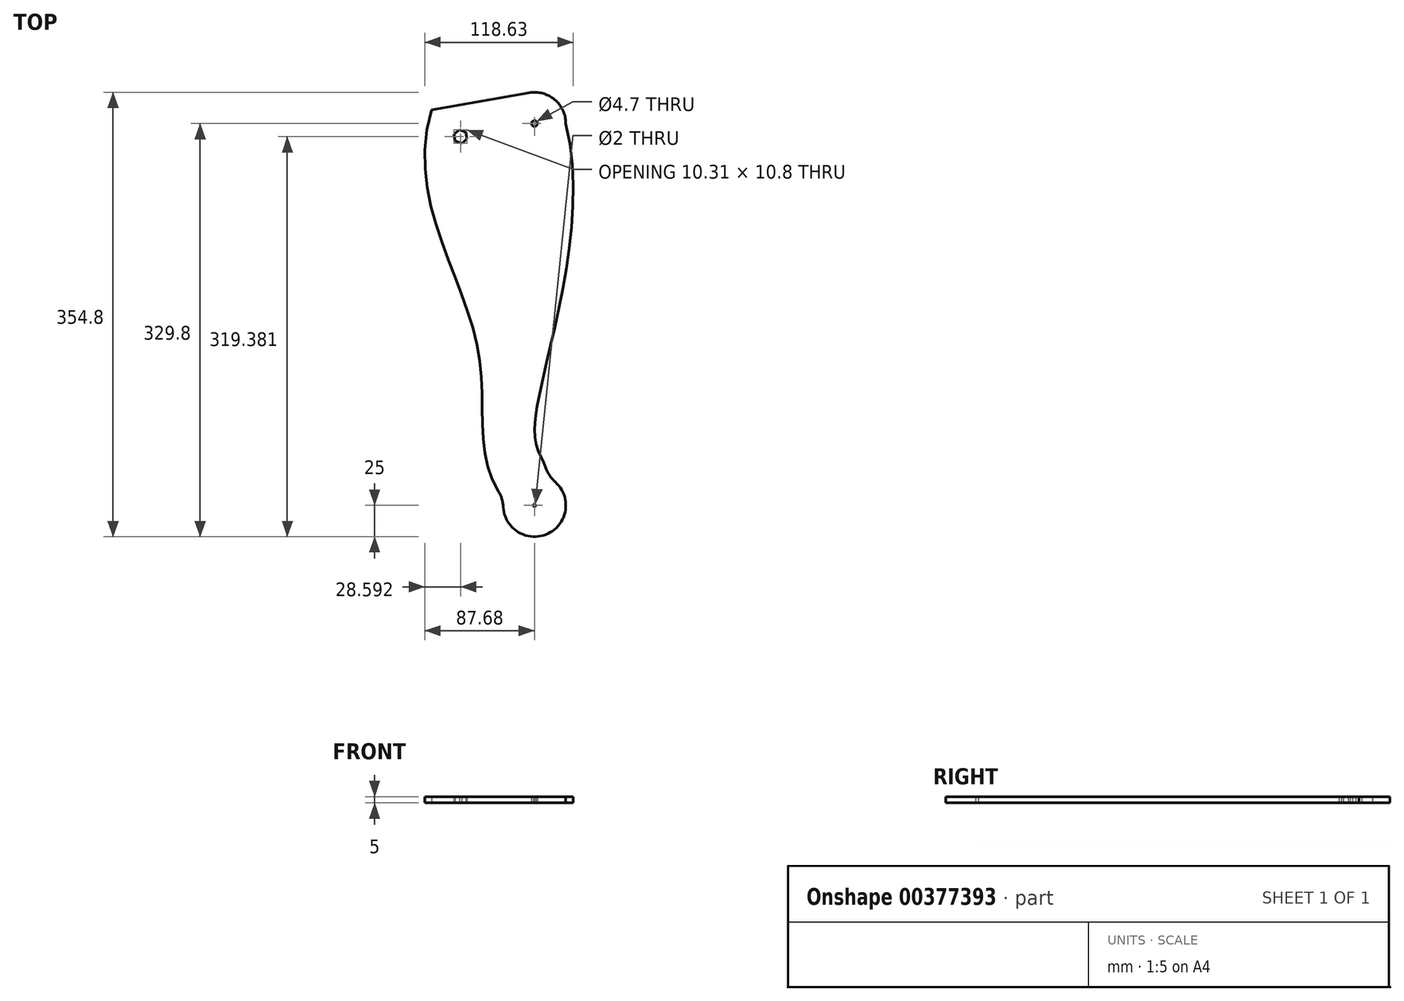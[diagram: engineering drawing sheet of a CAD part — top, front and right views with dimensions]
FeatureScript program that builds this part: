
annotation { "Feature Type Name" : "Feature", "Feature Type Description" : "" }
export const myFeature = defineFeature(function(context is Context, id is Id, definition is map)
    precondition{}
    {
        {
            var Q0;
            Q0=qCreatedBy(makeId("Top.planeOp"),FACE);
            var sketch = newSketch(context, id + "F0", { "sketchPlane" : qUnion([Q0])});
            skCircle(sketch, "E0", {"center": v(0, 0) * mm, "radius": 2.35 * mm});
            skArc(sketch, "E1", {"start": v(-24.44, -299.53) * mm, "mid": v(10.45, -327.51) * mm, "end": v(11.9, -282.81) * mm});
            skArc(sketch, "E2", {"start": v(25, 0) * mm, "mid": v(16.07, 19.15) * mm, "end": v(-4.34, 24.62) * mm});
            skLineSegment(sketch, "E3", {"start": v(-4.34, 24.62) * mm, "end": v(-82.12, 10.9) * mm});
            skLineSegment(sketch, "E4", {"start": v(-87.68, 20.59) * mm, "end": v(-87.68, -140.16) * mm, "construction": true});
            skLineSegment(sketch, "E5", {"start": v(-24.44, -299.53) * mm, "end": v(11.9, -282.81) * mm, "construction": true});
            skCircle(sketch, "E6", {"center": v(0, -304.8) * mm, "radius": 1 * mm});
            skFitSpline(sketch, "E7", {"points": [v(25, 0) * mm, v(0, -244.2) * mm, v(11.9, -282.81) * mm], "startDerivative": vector(93.1, -381.9) * mm, "endDerivative": vector(50.34, -171.54) * mm});
            skFitSpline(sketch, "E8", {"points": [v(-82.12, 10.9) * mm, v(-45.47, -178.53) * mm, v(-24.44, -299.53) * mm], "startDerivative": vector(-115.76, -382.46) * mm, "endDerivative": vector(173.9, -207.44) * mm});
            skLineSegment(sketch, "E9", {"start": v(30.95, -10.57) * mm, "end": v(30.95, -105.63) * mm, "construction": true});
            skSolve(sketch);
        }
        {
            var Q0;
            Q0=qCreatedBy(makeId("Top.planeOp"),FACE);
            var sketch = newSketch(context, id + "F1", { "sketchPlane" : qUnion([Q0])});
            skLineSegment(sketch, "E10", {"start": v(0, 0) * mm, "end": v(-59.09, -10.42) * mm, "construction": true});
            skCircle(sketch, "E11", {"center": v(-59.09, -10.42) * mm, "radius": 3 * mm, "construction": true});
            skCircle(sketch, "E12.cCircle", {"center": v(-59.09, -10.42) * mm, "radius": 4.75 * mm, "construction": true});
            skLineSegment(sketch, "E12.0", {"start": v(-54.89, -6.9) * mm, "end": v(-53.93, -12.3) * mm});
            skLineSegment(sketch, "E12.1", {"start": v(-53.93, -12.3) * mm, "end": v(-58.14, -15.82) * mm});
            skLineSegment(sketch, "E12.2", {"start": v(-58.14, -15.82) * mm, "end": v(-63.3, -13.94) * mm});
            skLineSegment(sketch, "E12.3", {"start": v(-63.3, -13.94) * mm, "end": v(-64.24, -8.54) * mm});
            skLineSegment(sketch, "E12.4", {"start": v(-64.24, -8.54) * mm, "end": v(-60.04, -5.02) * mm});
            skLineSegment(sketch, "E12.5", {"start": v(-60.04, -5.02) * mm, "end": v(-54.89, -6.9) * mm});
            skPoint(sketch, "E12.0.midPoint", {"position": v(-54.41, -9.6) * mm});
            skSolve(sketch);
        }
        {
            var Q0;
            Q0=qSketchRegion(id+"F0",true);
            extrude(context, id + "F2", {"entities" : qUnion([Q0]), "depth" : 5 * mm});
        }
        {
            var Q0;
            Q0=qSketchRegion(id+"F1",true);
            extrude(context, id + "F3", {"entities" : qUnion([Q0]), "operationType" : NewBodyOperationType.REMOVE, "endBound" : BoundingType.THROUGH_ALL, "depth" : 25 * mm});
        }
        {
            var Q0;
            Q0=makeQuery(id+"F2.opExtrude","SWEPT_EDGE",EDGE,{"disambiguationData":[OSD([sQuery(id+"F0.wireOp",EDGE,"E1"),sQuery(id+"F0.wireOp",EDGE,"IRwkBBPc-iLYB-gRdi-gAcp-Ph2cs2GShcop")])]});
            var Q1;
            Q1=makeQuery(id+"F2.opExtrude","SWEPT_EDGE",EDGE,{"disambiguationData":[OSD([sQuery(id+"F0.wireOp",EDGE,"E1"),sQuery(id+"F0.wireOp",EDGE,"1044895b-140e-4190-b1e2-f8b0b1552d9c")])]});
            fillet(context, id + "F4", {"entities" : qUnion([Q0, Q1]), "radius" : 25 * mm, "tangentPropagation" : true, "allowEdgeOverflow" : false});
        }
    });
